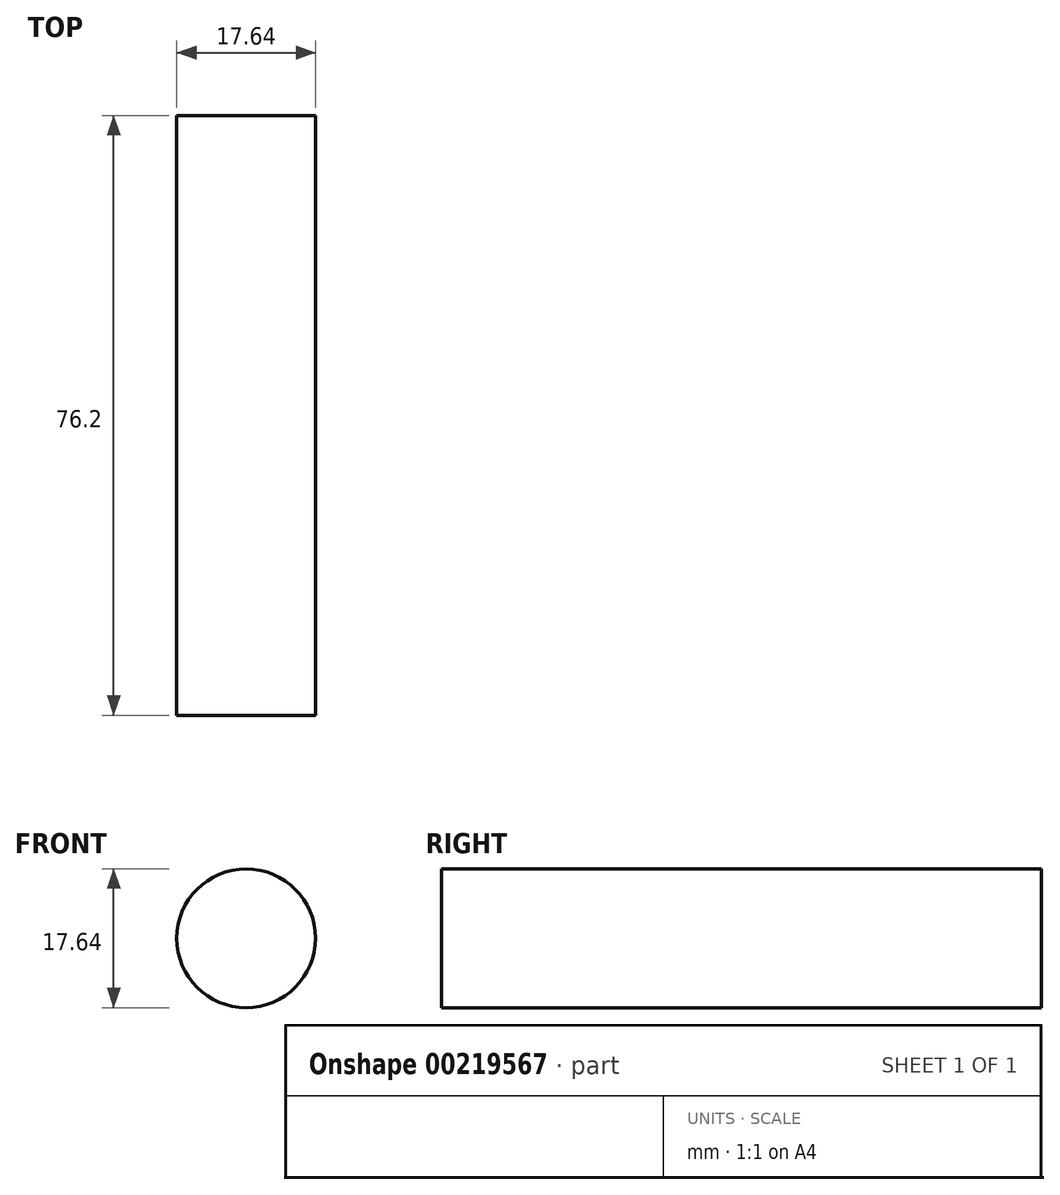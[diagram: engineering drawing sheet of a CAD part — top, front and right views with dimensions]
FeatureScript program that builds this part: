
annotation { "Feature Type Name" : "Feature", "Feature Type Description" : "" }
export const myFeature = defineFeature(function(context is Context, id is Id, definition is map)
    precondition{}
    {
        {
            var Q0;
            Q0=qCreatedBy(makeId("Front.planeOp"),FACE);
            var sketch = newSketch(context, id + "F0", { "sketchPlane" : qUnion([Q0])});
            skCircle(sketch, "E0", {"center": v(-80.22, 0) * mm, "radius": 8.82 * mm});
            skSolve(sketch);
        }
        {
            var Q0;
            Q0=makeQuery(id+"F0.imprint","IMPRINT",FACE,{"disambiguationData":[TD([[makeQuery(id+"F0.imprint","IMPRINT",EDGE,{"derivedFrom":sQuery(id+"F0.wireOp",EDGE,"E0")}),1.0]])]});
            extrude(context, id + "F1", {"entities" : qUnion([Q0]), "depth" : 76.2 * mm});
        }
    });
